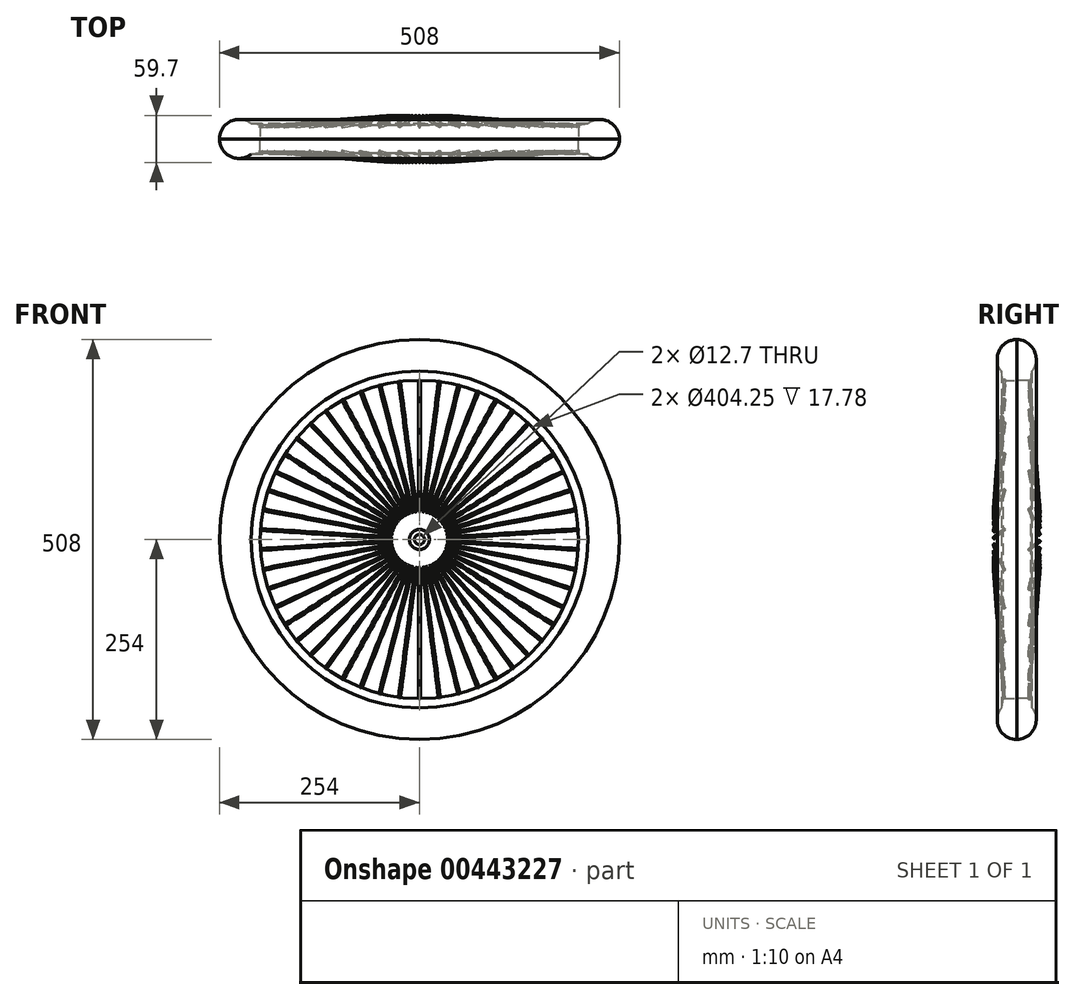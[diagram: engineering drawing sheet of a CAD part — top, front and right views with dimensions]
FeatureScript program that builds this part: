
annotation { "Feature Type Name" : "Feature", "Feature Type Description" : "" }
export const myFeature = defineFeature(function(context is Context, id is Id, definition is map)
    precondition{}
    {
        {
            var Q0;
            Q0=qCreatedBy(makeId("Right.planeOp"),FACE);
            var sketch = newSketch(context, id + "F0", { "sketchPlane" : qUnion([Q0])});
            skLineSegment(sketch, "E0", {"start": v(0, 0) * mm, "end": v(0, 82.93) * mm, "construction": true});
            skLineSegment(sketch, "E1", {"start": v(0, 0) * mm, "end": v(-55.04, 0) * mm, "construction": true});
            skArc(sketch, "E2", {"start": v(0, 254) * mm, "mid": v(-22.29, 240.03) * mm, "end": v(-19.43, 213.88) * mm});
            skLineSegment(sketch, "E3", {"start": v(0, 202.13) * mm, "end": v(-17.78, 202.13) * mm});
            skLineSegment(sketch, "E4", {"start": v(-21.6, 229.23) * mm, "end": v(0, 229.23) * mm, "construction": true});
            skLineSegment(sketch, "E5", {"start": v(-21.59, 229.23) * mm, "end": v(-17.78, 202.13) * mm, "construction": true});
            skLineSegment(sketch, "E6", {"start": v(0, 229.23) * mm, "end": v(0, 173.52) * mm, "construction": true});
            skLineSegment(sketch, "E7", {"start": v(-19.43, 213.88) * mm, "end": v(-17.78, 202.13) * mm});
            skLineSegment(sketch, "E8", {"start": v(0, 202.13) * mm, "end": v(0, 254) * mm});
            skPoint(sketch, "E9.end.orphan", {"position": v(17.78, 202.13) * mm});
            skPoint(sketch, "E10.orphan", {"position": v(21.6, 229.24) * mm});
            skSolve(sketch);
        }
        {
            var Q0;
            Q0 = qSketchRegion(id + "F0", true);
            var Q1;
            Q1=sQuery(id+"F0.wireOp",EDGE,"E1");
            revolve(context, id + "F1", {"entities" : qUnion([Q0]), "axis" : qUnion([Q1]), "revolveType" : RevolveType.FULL});
        }
        {
            var Q0;
            Q0=qCreatedBy(makeId("Front.planeOp"),FACE);
            var sketch = newSketch(context, id + "F2", { "sketchPlane" : qUnion([Q0])});
            skCircle(sketch, "E11", {"center": v(0, 0) * mm, "radius": 6.35 * mm});
            skCircle(sketch, "E12", {"center": v(0, 0) * mm, "radius": 12.7 * mm});
            skCircle(sketch, "E13", {"center": v(0, 0) * mm, "radius": 38.1 * mm});
            skSolve(sketch);
        }
        {
            var Q0;
            Q0=makeQuery(id+"F2.imprint","IMPRINT",FACE,{"disambiguationData":[TD([[makeQuery(id+"F2.imprint","IMPRINT",EDGE,{"derivedFrom":sQuery(id+"F2.wireOp",EDGE,"E11")}),-1.0]])]});
            extrude(context, id + "F3", {"entities" : qUnion([Q0]), "flatOperationType" : FlatOperationType.REMOVE, "offsetDistance" : 25.4 * mm, "depth" : 2.5 / 50.8 * mm, "domain" : OperationDomain.MODEL});
        }
        {
            var Q0;
            Q0 = qSketchRegion(id + "F2", true);
            var Q1;
            Q1=makeQuery(id+"F3.opExtrude","CAP_FACE",FACE,{"disambiguationData":[OSD([sQuery(id+"F2.wireOp",EDGE,"E11"),sQuery(id+"F2.wireOp",EDGE,"E12")])],"isStart":false});
            extrude(context, id + "F4", {"entities" : qUnion([Q0]), "operationType" : NewBodyOperationType.ADD, "endBoundEntityFace" : qUnion([Q1]), "depth" : 2.5 / 50.8 * mm});
        }
        {
            var Q0;
            Q0 = qSketchRegion(id + "F2", true);
            extrude(context, id + "F5", {"entities" : qUnion([Q0]), "operationType" : NewBodyOperationType.REMOVE, "depth" : 25.4 * mm});
        }
        {
            var Q0;
            Q0=qCreatedBy(makeId("Right.planeOp"),FACE);
            var sketch = newSketch(context, id + "F6", { "sketchPlane" : qUnion([Q0])});
            skLineSegment(sketch, "E14", {"start": v(-15.87, 205.94) * mm, "end": v(-28.58, 38.1) * mm});
            skLineSegment(sketch, "E15", {"start": v(0, 205.94) * mm, "end": v(-15.87, 205.94) * mm, "construction": true});
            skLineSegment(sketch, "E16", {"start": v(-28.58, 38.1) * mm, "end": v(0, 38.1) * mm, "construction": true});
            skLineSegment(sketch, "E17", {"start": v(0, -3.25) * mm, "end": v(0, 205.94) * mm, "construction": true});
            skPoint(sketch, "E18.orphan", {"position": v(15.87, 205.94) * mm});
            skSolve(sketch);
        }
        {
            var Q0;
            Q0=qCreatedBy(makeId("Top.planeOp"),FACE);
            cPlane(context, id + "F7", {"entities" : qUnion([Q0]), "cplaneType" : CPlaneType.OFFSET, "offset" : 35.56 * mm, "width" : 152.4 * mm, "height" : 152.4 * mm});
        }
        {
            var Q0;
            Q0=qCreatedBy(id+"F7.planeOp",FACE);
            var sketch = newSketch(context, id + "F8", { "sketchPlane" : qUnion([Q0])});
            skCircle(sketch, "E19", {"center": v(0, -28.58) * mm, "radius": 1.27 * mm});
            skSolve(sketch);
        }
        {
            var Q0;
            Q0 = qSketchRegion(id + "F8", true);
            var Q1;
            Q1=sQuery(id+"F6.wireOp",EDGE,"E14");
            sweep(context, id + "F9", {"profiles" : qUnion([Q0]), "path" : qUnion([Q1])});
        }
        {
            var Q0;
            Q0=makeQuery(id+"F9.opSweep","SWEPT_BODY",BODY,{"disambiguationData":[OSD([sQuery(id+"F6.wireOp",EDGE,"E14"),sQuery(id+"F8.wireOp",EDGE,"E19")])]});
            var Q1;
            Q1=sQuery(id+"F0.wireOp",EDGE,"E1");
            circularPattern(context, id + "F10", {"entities" : qUnion([Q0]), "axis" : qUnion([Q1]), "angle" : 360 * degree, "instanceCount" : 25, "equalSpace" : true});
        }
        {
            var Q0;
            Q0=makeQuery(id+"F10.opPattern","COPY",BODY,{"derivedFrom":makeQuery(id+"F9.opSweep","SWEPT_BODY",BODY,{"disambiguationData":[OSD([sQuery(id+"F6.wireOp",EDGE,"E14"),sQuery(id+"F8.wireOp",EDGE,"E19")])]}),"instanceName":"24"});
            var Q1;
            Q1=makeQuery(id+"F10.opPattern","COPY",BODY,{"derivedFrom":makeQuery(id+"F9.opSweep","SWEPT_BODY",BODY,{"disambiguationData":[OSD([sQuery(id+"F6.wireOp",EDGE,"E14"),sQuery(id+"F8.wireOp",EDGE,"E19")])]}),"instanceName":"11"});
            var Q2;
            Q2=makeQuery(id+"F10.opPattern","COPY",BODY,{"derivedFrom":makeQuery(id+"F9.opSweep","SWEPT_BODY",BODY,{"disambiguationData":[OSD([sQuery(id+"F6.wireOp",EDGE,"E14"),sQuery(id+"F8.wireOp",EDGE,"E19")])]}),"instanceName":"10"});
            var Q3;
            Q3=makeQuery(id+"F10.opPattern","COPY",BODY,{"derivedFrom":makeQuery(id+"F9.opSweep","SWEPT_BODY",BODY,{"disambiguationData":[OSD([sQuery(id+"F6.wireOp",EDGE,"E14"),sQuery(id+"F8.wireOp",EDGE,"E19")])]}),"instanceName":"3"});
            var Q4;
            Q4=makeQuery(id+"F10.opPattern","COPY",BODY,{"derivedFrom":makeQuery(id+"F9.opSweep","SWEPT_BODY",BODY,{"disambiguationData":[OSD([sQuery(id+"F6.wireOp",EDGE,"E14"),sQuery(id+"F8.wireOp",EDGE,"E19")])]}),"instanceName":"5"});
            var Q5;
            Q5=makeQuery(id+"F10.opPattern","COPY",BODY,{"derivedFrom":makeQuery(id+"F9.opSweep","SWEPT_BODY",BODY,{"disambiguationData":[OSD([sQuery(id+"F6.wireOp",EDGE,"E14"),sQuery(id+"F8.wireOp",EDGE,"E19")])]}),"instanceName":"13"});
            var Q6;
            Q6=makeQuery(id+"F10.opPattern","COPY",BODY,{"derivedFrom":makeQuery(id+"F9.opSweep","SWEPT_BODY",BODY,{"disambiguationData":[OSD([sQuery(id+"F6.wireOp",EDGE,"E14"),sQuery(id+"F8.wireOp",EDGE,"E19")])]}),"instanceName":"21"});
            var Q7;
            Q7=makeQuery(id+"F10.opPattern","COPY",BODY,{"derivedFrom":makeQuery(id+"F9.opSweep","SWEPT_BODY",BODY,{"disambiguationData":[OSD([sQuery(id+"F6.wireOp",EDGE,"E14"),sQuery(id+"F8.wireOp",EDGE,"E19")])]}),"instanceName":"14"});
            var Q8;
            Q8=makeQuery(id+"F10.opPattern","COPY",BODY,{"derivedFrom":makeQuery(id+"F9.opSweep","SWEPT_BODY",BODY,{"disambiguationData":[OSD([sQuery(id+"F6.wireOp",EDGE,"E14"),sQuery(id+"F8.wireOp",EDGE,"E19")])]}),"instanceName":"15"});
            var Q9;
            Q9=makeQuery(id+"F9.opSweep","SWEPT_BODY",BODY,{"disambiguationData":[OSD([sQuery(id+"F6.wireOp",EDGE,"E14"),sQuery(id+"F8.wireOp",EDGE,"E19")])]});
            var Q10;
            Q10=makeQuery(id+"F10.opPattern","COPY",BODY,{"derivedFrom":makeQuery(id+"F9.opSweep","SWEPT_BODY",BODY,{"disambiguationData":[OSD([sQuery(id+"F6.wireOp",EDGE,"E14"),sQuery(id+"F8.wireOp",EDGE,"E19")])]}),"instanceName":"4"});
            var Q11;
            Q11=makeQuery(id+"F10.opPattern","COPY",BODY,{"derivedFrom":makeQuery(id+"F9.opSweep","SWEPT_BODY",BODY,{"disambiguationData":[OSD([sQuery(id+"F6.wireOp",EDGE,"E14"),sQuery(id+"F8.wireOp",EDGE,"E19")])]}),"instanceName":"16"});
            var Q12;
            Q12=makeQuery(id+"F10.opPattern","COPY",BODY,{"derivedFrom":makeQuery(id+"F9.opSweep","SWEPT_BODY",BODY,{"disambiguationData":[OSD([sQuery(id+"F6.wireOp",EDGE,"E14"),sQuery(id+"F8.wireOp",EDGE,"E19")])]}),"instanceName":"20"});
            var Q13;
            Q13=makeQuery(id+"F10.opPattern","COPY",BODY,{"derivedFrom":makeQuery(id+"F9.opSweep","SWEPT_BODY",BODY,{"disambiguationData":[OSD([sQuery(id+"F6.wireOp",EDGE,"E14"),sQuery(id+"F8.wireOp",EDGE,"E19")])]}),"instanceName":"17"});
            var Q14;
            Q14=makeQuery(id+"F10.opPattern","COPY",BODY,{"derivedFrom":makeQuery(id+"F9.opSweep","SWEPT_BODY",BODY,{"disambiguationData":[OSD([sQuery(id+"F6.wireOp",EDGE,"E14"),sQuery(id+"F8.wireOp",EDGE,"E19")])]}),"instanceName":"6"});
            var Q15;
            Q15=makeQuery(id+"F10.opPattern","COPY",BODY,{"derivedFrom":makeQuery(id+"F9.opSweep","SWEPT_BODY",BODY,{"disambiguationData":[OSD([sQuery(id+"F6.wireOp",EDGE,"E14"),sQuery(id+"F8.wireOp",EDGE,"E19")])]}),"instanceName":"7"});
            var Q16;
            Q16=makeQuery(id+"F10.opPattern","COPY",BODY,{"derivedFrom":makeQuery(id+"F9.opSweep","SWEPT_BODY",BODY,{"disambiguationData":[OSD([sQuery(id+"F6.wireOp",EDGE,"E14"),sQuery(id+"F8.wireOp",EDGE,"E19")])]}),"instanceName":"2"});
            var Q17;
            Q17=makeQuery(id+"F10.opPattern","COPY",BODY,{"derivedFrom":makeQuery(id+"F9.opSweep","SWEPT_BODY",BODY,{"disambiguationData":[OSD([sQuery(id+"F6.wireOp",EDGE,"E14"),sQuery(id+"F8.wireOp",EDGE,"E19")])]}),"instanceName":"22"});
            var Q18;
            Q18=makeQuery(id+"F10.opPattern","COPY",BODY,{"derivedFrom":makeQuery(id+"F9.opSweep","SWEPT_BODY",BODY,{"disambiguationData":[OSD([sQuery(id+"F6.wireOp",EDGE,"E14"),sQuery(id+"F8.wireOp",EDGE,"E19")])]}),"instanceName":"8"});
            var Q19;
            Q19=makeQuery(id+"F10.opPattern","COPY",BODY,{"derivedFrom":makeQuery(id+"F9.opSweep","SWEPT_BODY",BODY,{"disambiguationData":[OSD([sQuery(id+"F6.wireOp",EDGE,"E14"),sQuery(id+"F8.wireOp",EDGE,"E19")])]}),"instanceName":"9"});
            var Q20;
            Q20=makeQuery(id+"F10.opPattern","COPY",BODY,{"derivedFrom":makeQuery(id+"F9.opSweep","SWEPT_BODY",BODY,{"disambiguationData":[OSD([sQuery(id+"F6.wireOp",EDGE,"E14"),sQuery(id+"F8.wireOp",EDGE,"E19")])]}),"instanceName":"19"});
            var Q21;
            Q21=makeQuery(id+"F10.opPattern","COPY",BODY,{"derivedFrom":makeQuery(id+"F9.opSweep","SWEPT_BODY",BODY,{"disambiguationData":[OSD([sQuery(id+"F6.wireOp",EDGE,"E14"),sQuery(id+"F8.wireOp",EDGE,"E19")])]}),"instanceName":"18"});
            var Q22;
            Q22=makeQuery(id+"F3.opExtrude","SWEPT_BODY",BODY,{"disambiguationData":[OSD([sQuery(id+"F2.wireOp",EDGE,"E11"),sQuery(id+"F2.wireOp",EDGE,"E12")])]});
            var Q23;
            Q23=makeQuery(id+"F10.opPattern","COPY",BODY,{"derivedFrom":makeQuery(id+"F9.opSweep","SWEPT_BODY",BODY,{"disambiguationData":[OSD([sQuery(id+"F6.wireOp",EDGE,"E14"),sQuery(id+"F8.wireOp",EDGE,"E19")])]}),"instanceName":"12"});
            var Q24;
            Q24=makeQuery(id+"F1.opRevolve","SWEPT_BODY",BODY,{"disambiguationData":[OSD([sQuery(id+"F0.wireOp",EDGE,"E2"),sQuery(id+"F0.wireOp",EDGE,"E3"),sQuery(id+"F0.wireOp",EDGE,"E7"),sQuery(id+"F0.wireOp",EDGE,"E8")])]});
            var Q25;
            Q25=makeQuery(id+"F10.opPattern","COPY",BODY,{"derivedFrom":makeQuery(id+"F9.opSweep","SWEPT_BODY",BODY,{"disambiguationData":[OSD([sQuery(id+"F6.wireOp",EDGE,"E14"),sQuery(id+"F8.wireOp",EDGE,"E19")])]}),"instanceName":"1"});
            var Q26;
            Q26=makeQuery(id+"F10.opPattern","COPY",BODY,{"derivedFrom":makeQuery(id+"F9.opSweep","SWEPT_BODY",BODY,{"disambiguationData":[OSD([sQuery(id+"F6.wireOp",EDGE,"E14"),sQuery(id+"F8.wireOp",EDGE,"E19")])]}),"instanceName":"23"});
            var Q27;
            Q27=qCreatedBy(makeId("Front.planeOp"),FACE);
            mirror(context, id + "F11", {"entities" : qUnion([Q0, Q1, Q2, Q3, Q4, Q5, Q6, Q7, Q8, Q9, Q10, Q11, Q12, Q13, Q14, Q15, Q16, Q17, Q18, Q19, Q20, Q21, Q22, Q23, Q24, Q25, Q26]), "mirrorPlane" : qUnion([Q27])});
        }
        {
            var Q0;
            Q0=makeQuery(id+"F11.opPattern","COPY",BODY,{"derivedFrom":makeQuery(id+"F1.opRevolve","SWEPT_BODY",BODY,{"disambiguationData":[OSD([sQuery(id+"F0.wireOp",EDGE,"E2"),sQuery(id+"F0.wireOp",EDGE,"E3"),sQuery(id+"F0.wireOp",EDGE,"E7"),sQuery(id+"F0.wireOp",EDGE,"E8")])]}),"instanceName":"1"});
            var Q1;
            Q1=makeQuery(id+"F11.opPattern","COPY",BODY,{"derivedFrom":makeQuery(id+"F3.opExtrude","SWEPT_BODY",BODY,{"disambiguationData":[OSD([sQuery(id+"F2.wireOp",EDGE,"E11"),sQuery(id+"F2.wireOp",EDGE,"E12")])]}),"instanceName":"1"});
            var Q2;
            Q2=makeQuery(id+"F11.opPattern","COPY",BODY,{"derivedFrom":makeQuery(id+"F9.opSweep","SWEPT_BODY",BODY,{"disambiguationData":[OSD([sQuery(id+"F6.wireOp",EDGE,"E14"),sQuery(id+"F8.wireOp",EDGE,"E19")])]}),"instanceName":"1"});
            var Q3;
            Q3=makeQuery(id+"F11.opPattern","COPY",BODY,{"derivedFrom":makeQuery(id+"F10.opPattern","COPY",BODY,{"derivedFrom":makeQuery(id+"F9.opSweep","SWEPT_BODY",BODY,{"disambiguationData":[OSD([sQuery(id+"F6.wireOp",EDGE,"E14"),sQuery(id+"F8.wireOp",EDGE,"E19")])]}),"instanceName":"1"}),"instanceName":"1"});
            var Q4;
            Q4=makeQuery(id+"F11.opPattern","COPY",BODY,{"derivedFrom":makeQuery(id+"F10.opPattern","COPY",BODY,{"derivedFrom":makeQuery(id+"F9.opSweep","SWEPT_BODY",BODY,{"disambiguationData":[OSD([sQuery(id+"F6.wireOp",EDGE,"E14"),sQuery(id+"F8.wireOp",EDGE,"E19")])]}),"instanceName":"2"}),"instanceName":"1"});
            var Q5;
            Q5=makeQuery(id+"F11.opPattern","COPY",BODY,{"derivedFrom":makeQuery(id+"F10.opPattern","COPY",BODY,{"derivedFrom":makeQuery(id+"F9.opSweep","SWEPT_BODY",BODY,{"disambiguationData":[OSD([sQuery(id+"F6.wireOp",EDGE,"E14"),sQuery(id+"F8.wireOp",EDGE,"E19")])]}),"instanceName":"3"}),"instanceName":"1"});
            var Q6;
            Q6=makeQuery(id+"F11.opPattern","COPY",BODY,{"derivedFrom":makeQuery(id+"F10.opPattern","COPY",BODY,{"derivedFrom":makeQuery(id+"F9.opSweep","SWEPT_BODY",BODY,{"disambiguationData":[OSD([sQuery(id+"F6.wireOp",EDGE,"E14"),sQuery(id+"F8.wireOp",EDGE,"E19")])]}),"instanceName":"4"}),"instanceName":"1"});
            var Q7;
            Q7=makeQuery(id+"F11.opPattern","COPY",BODY,{"derivedFrom":makeQuery(id+"F10.opPattern","COPY",BODY,{"derivedFrom":makeQuery(id+"F9.opSweep","SWEPT_BODY",BODY,{"disambiguationData":[OSD([sQuery(id+"F6.wireOp",EDGE,"E14"),sQuery(id+"F8.wireOp",EDGE,"E19")])]}),"instanceName":"5"}),"instanceName":"1"});
            var Q8;
            Q8=makeQuery(id+"F11.opPattern","COPY",BODY,{"derivedFrom":makeQuery(id+"F10.opPattern","COPY",BODY,{"derivedFrom":makeQuery(id+"F9.opSweep","SWEPT_BODY",BODY,{"disambiguationData":[OSD([sQuery(id+"F6.wireOp",EDGE,"E14"),sQuery(id+"F8.wireOp",EDGE,"E19")])]}),"instanceName":"6"}),"instanceName":"1"});
            var Q9;
            Q9=makeQuery(id+"F11.opPattern","COPY",BODY,{"derivedFrom":makeQuery(id+"F10.opPattern","COPY",BODY,{"derivedFrom":makeQuery(id+"F9.opSweep","SWEPT_BODY",BODY,{"disambiguationData":[OSD([sQuery(id+"F6.wireOp",EDGE,"E14"),sQuery(id+"F8.wireOp",EDGE,"E19")])]}),"instanceName":"7"}),"instanceName":"1"});
            var Q10;
            Q10=makeQuery(id+"F11.opPattern","COPY",BODY,{"derivedFrom":makeQuery(id+"F10.opPattern","COPY",BODY,{"derivedFrom":makeQuery(id+"F9.opSweep","SWEPT_BODY",BODY,{"disambiguationData":[OSD([sQuery(id+"F6.wireOp",EDGE,"E14"),sQuery(id+"F8.wireOp",EDGE,"E19")])]}),"instanceName":"8"}),"instanceName":"1"});
            var Q11;
            Q11=makeQuery(id+"F11.opPattern","COPY",BODY,{"derivedFrom":makeQuery(id+"F10.opPattern","COPY",BODY,{"derivedFrom":makeQuery(id+"F9.opSweep","SWEPT_BODY",BODY,{"disambiguationData":[OSD([sQuery(id+"F6.wireOp",EDGE,"E14"),sQuery(id+"F8.wireOp",EDGE,"E19")])]}),"instanceName":"9"}),"instanceName":"1"});
            var Q12;
            Q12=makeQuery(id+"F11.opPattern","COPY",BODY,{"derivedFrom":makeQuery(id+"F10.opPattern","COPY",BODY,{"derivedFrom":makeQuery(id+"F9.opSweep","SWEPT_BODY",BODY,{"disambiguationData":[OSD([sQuery(id+"F6.wireOp",EDGE,"E14"),sQuery(id+"F8.wireOp",EDGE,"E19")])]}),"instanceName":"10"}),"instanceName":"1"});
            var Q13;
            Q13=makeQuery(id+"F11.opPattern","COPY",BODY,{"derivedFrom":makeQuery(id+"F10.opPattern","COPY",BODY,{"derivedFrom":makeQuery(id+"F9.opSweep","SWEPT_BODY",BODY,{"disambiguationData":[OSD([sQuery(id+"F6.wireOp",EDGE,"E14"),sQuery(id+"F8.wireOp",EDGE,"E19")])]}),"instanceName":"11"}),"instanceName":"1"});
            var Q14;
            Q14=makeQuery(id+"F11.opPattern","COPY",BODY,{"derivedFrom":makeQuery(id+"F10.opPattern","COPY",BODY,{"derivedFrom":makeQuery(id+"F9.opSweep","SWEPT_BODY",BODY,{"disambiguationData":[OSD([sQuery(id+"F6.wireOp",EDGE,"E14"),sQuery(id+"F8.wireOp",EDGE,"E19")])]}),"instanceName":"12"}),"instanceName":"1"});
            var Q15;
            Q15=makeQuery(id+"F11.opPattern","COPY",BODY,{"derivedFrom":makeQuery(id+"F10.opPattern","COPY",BODY,{"derivedFrom":makeQuery(id+"F9.opSweep","SWEPT_BODY",BODY,{"disambiguationData":[OSD([sQuery(id+"F6.wireOp",EDGE,"E14"),sQuery(id+"F8.wireOp",EDGE,"E19")])]}),"instanceName":"13"}),"instanceName":"1"});
            var Q16;
            Q16=makeQuery(id+"F11.opPattern","COPY",BODY,{"derivedFrom":makeQuery(id+"F10.opPattern","COPY",BODY,{"derivedFrom":makeQuery(id+"F9.opSweep","SWEPT_BODY",BODY,{"disambiguationData":[OSD([sQuery(id+"F6.wireOp",EDGE,"E14"),sQuery(id+"F8.wireOp",EDGE,"E19")])]}),"instanceName":"14"}),"instanceName":"1"});
            var Q17;
            Q17=makeQuery(id+"F11.opPattern","COPY",BODY,{"derivedFrom":makeQuery(id+"F10.opPattern","COPY",BODY,{"derivedFrom":makeQuery(id+"F9.opSweep","SWEPT_BODY",BODY,{"disambiguationData":[OSD([sQuery(id+"F6.wireOp",EDGE,"E14"),sQuery(id+"F8.wireOp",EDGE,"E19")])]}),"instanceName":"15"}),"instanceName":"1"});
            var Q18;
            Q18=makeQuery(id+"F11.opPattern","COPY",BODY,{"derivedFrom":makeQuery(id+"F10.opPattern","COPY",BODY,{"derivedFrom":makeQuery(id+"F9.opSweep","SWEPT_BODY",BODY,{"disambiguationData":[OSD([sQuery(id+"F6.wireOp",EDGE,"E14"),sQuery(id+"F8.wireOp",EDGE,"E19")])]}),"instanceName":"16"}),"instanceName":"1"});
            var Q19;
            Q19=makeQuery(id+"F11.opPattern","COPY",BODY,{"derivedFrom":makeQuery(id+"F10.opPattern","COPY",BODY,{"derivedFrom":makeQuery(id+"F9.opSweep","SWEPT_BODY",BODY,{"disambiguationData":[OSD([sQuery(id+"F6.wireOp",EDGE,"E14"),sQuery(id+"F8.wireOp",EDGE,"E19")])]}),"instanceName":"17"}),"instanceName":"1"});
            var Q20;
            Q20=makeQuery(id+"F11.opPattern","COPY",BODY,{"derivedFrom":makeQuery(id+"F10.opPattern","COPY",BODY,{"derivedFrom":makeQuery(id+"F9.opSweep","SWEPT_BODY",BODY,{"disambiguationData":[OSD([sQuery(id+"F6.wireOp",EDGE,"E14"),sQuery(id+"F8.wireOp",EDGE,"E19")])]}),"instanceName":"18"}),"instanceName":"1"});
            var Q21;
            Q21=makeQuery(id+"F11.opPattern","COPY",BODY,{"derivedFrom":makeQuery(id+"F10.opPattern","COPY",BODY,{"derivedFrom":makeQuery(id+"F9.opSweep","SWEPT_BODY",BODY,{"disambiguationData":[OSD([sQuery(id+"F6.wireOp",EDGE,"E14"),sQuery(id+"F8.wireOp",EDGE,"E19")])]}),"instanceName":"19"}),"instanceName":"1"});
            var Q22;
            Q22=makeQuery(id+"F11.opPattern","COPY",BODY,{"derivedFrom":makeQuery(id+"F10.opPattern","COPY",BODY,{"derivedFrom":makeQuery(id+"F9.opSweep","SWEPT_BODY",BODY,{"disambiguationData":[OSD([sQuery(id+"F6.wireOp",EDGE,"E14"),sQuery(id+"F8.wireOp",EDGE,"E19")])]}),"instanceName":"20"}),"instanceName":"1"});
            var Q23;
            Q23=makeQuery(id+"F11.opPattern","COPY",BODY,{"derivedFrom":makeQuery(id+"F10.opPattern","COPY",BODY,{"derivedFrom":makeQuery(id+"F9.opSweep","SWEPT_BODY",BODY,{"disambiguationData":[OSD([sQuery(id+"F6.wireOp",EDGE,"E14"),sQuery(id+"F8.wireOp",EDGE,"E19")])]}),"instanceName":"21"}),"instanceName":"1"});
            var Q24;
            Q24=makeQuery(id+"F11.opPattern","COPY",BODY,{"derivedFrom":makeQuery(id+"F10.opPattern","COPY",BODY,{"derivedFrom":makeQuery(id+"F9.opSweep","SWEPT_BODY",BODY,{"disambiguationData":[OSD([sQuery(id+"F6.wireOp",EDGE,"E14"),sQuery(id+"F8.wireOp",EDGE,"E19")])]}),"instanceName":"22"}),"instanceName":"1"});
            var Q25;
            Q25=makeQuery(id+"F11.opPattern","COPY",BODY,{"derivedFrom":makeQuery(id+"F10.opPattern","COPY",BODY,{"derivedFrom":makeQuery(id+"F9.opSweep","SWEPT_BODY",BODY,{"disambiguationData":[OSD([sQuery(id+"F6.wireOp",EDGE,"E14"),sQuery(id+"F8.wireOp",EDGE,"E19")])]}),"instanceName":"23"}),"instanceName":"1"});
            var Q26;
            Q26=makeQuery(id+"F11.opPattern","COPY",BODY,{"derivedFrom":makeQuery(id+"F10.opPattern","COPY",BODY,{"derivedFrom":makeQuery(id+"F9.opSweep","SWEPT_BODY",BODY,{"disambiguationData":[OSD([sQuery(id+"F6.wireOp",EDGE,"E14"),sQuery(id+"F8.wireOp",EDGE,"E19")])]}),"instanceName":"24"}),"instanceName":"1"});
            var Q27;
            Q27=sQuery(id+"F0.wireOp",EDGE,"E1");
            transform(context, id + "F12", {"entities" : qUnion([Q0, Q1, Q2, Q3, Q4, Q5, Q6, Q7, Q8, Q9, Q10, Q11, Q12, Q13, Q14, Q15, Q16, Q17, Q18, Q19, Q20, Q21, Q22, Q23, Q24, Q25, Q26]), "transformType" : TransformType.ROTATION, "transformAxis" : qUnion([Q27]), "angle" : 7.2 * degree, "makeCopy" : false});
        }
    });
